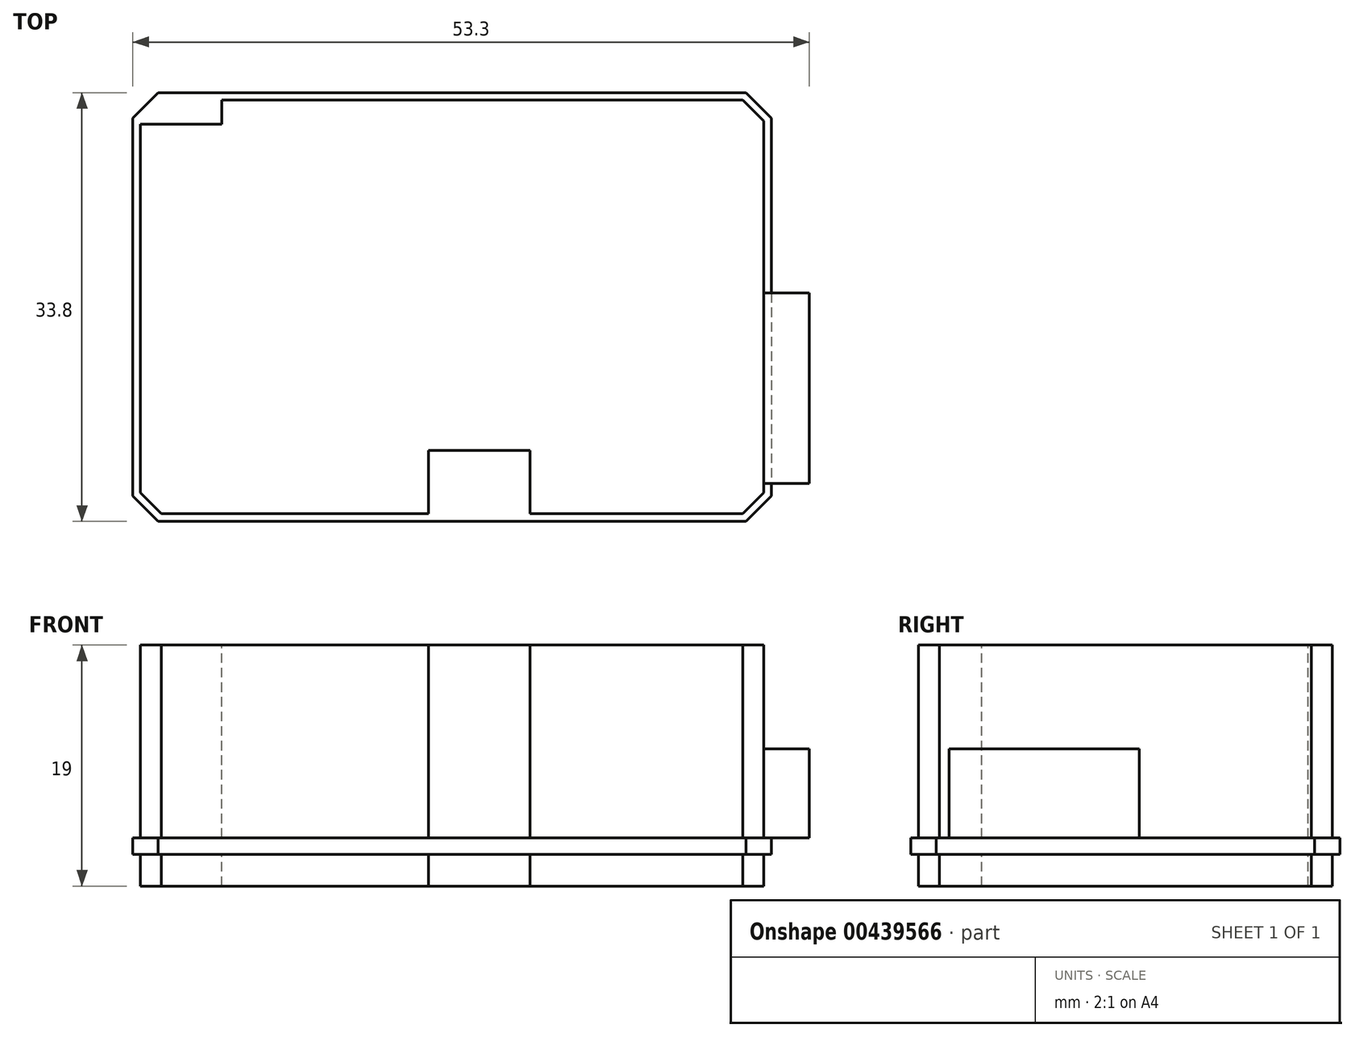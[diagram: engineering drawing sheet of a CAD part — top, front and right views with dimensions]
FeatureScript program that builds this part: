
annotation { "Feature Type Name" : "Feature", "Feature Type Description" : "" }
export const myFeature = defineFeature(function(context is Context, id is Id, definition is map)
    precondition{}
    {
        {
            var Q0;
            Q0=qCreatedBy(makeId("Top.planeOp"),FACE);
            var sketch = newSketch(context, id + "F0", { "sketchPlane" : qUnion([Q0])});
            skLineSegment(sketch, "E0.bottom", {"start": v(22.3, -100) * mm, "end": v(22.3, -133.8) * mm});
            skLineSegment(sketch, "E0.top", {"start": v(-28, -100) * mm, "end": v(-28, -133.8) * mm});
            skLineSegment(sketch, "E0.left", {"start": v(22.3, -100) * mm, "end": v(-28, -100) * mm});
            skLineSegment(sketch, "E0.right", {"start": v(22.3, -133.8) * mm, "end": v(-28, -133.8) * mm});
            skLineSegment(sketch, "E1.bottom", {"start": v(25.3, -115.8) * mm, "end": v(25.3, -130.8) * mm});
            skLineSegment(sketch, "E1.top", {"start": v(11.3, -115.8) * mm, "end": v(11.3, -130.8) * mm});
            skLineSegment(sketch, "E1.left", {"start": v(25.3, -115.8) * mm, "end": v(11.3, -115.8) * mm});
            skLineSegment(sketch, "E1.right", {"start": v(25.3, -130.8) * mm, "end": v(11.3, -130.8) * mm});
            skLineSegment(sketch, "E2", {"start": v(0, 0) * mm, "end": v(0, -100) * mm, "construction": true});
            skSolve(sketch);
        }
        {
            var Q0;
            Q0=makeQuery(id+"F0.imprint","IMPRINT",FACE,{"disambiguationData":[TD([[makeQuery(id+"F0.imprint","IMPRINT",EDGE,{"derivedFrom":sQuery(id+"F0.wireOp",EDGE,"E0.top")}),1.0]])]});
            var Q1;
            {var subQ5=sQuery(id+"F0.wireOp",EDGE,"E1.top");Q1=makeQuery(id+"F0.imprint","IMPRINT",FACE,{"disambiguationData":[TD([[makeQuery(id+"F0.imprint","IMPRINT",EDGE,{"derivedFrom":subQ5}),1.0]])]});}
            extrude(context, id + "F1", {"entities" : qUnion([Q0, Q1]), "oppositeDirection" : true, "depth" : 1.3 * mm});
        }
        {
            var Q0;
            {var subQ5=sQuery(id+"F0.wireOp",EDGE,"E1.bottom");Q0=makeQuery(id+"F0.imprint","IMPRINT",FACE,{"disambiguationData":[TD([[makeQuery(id+"F0.imprint","IMPRINT",EDGE,{"derivedFrom":subQ5}),-1.0]])]});}
            var Q1;
            {var subQ5=sQuery(id+"F0.wireOp",EDGE,"E1.top");Q1=makeQuery(id+"F0.imprint","IMPRINT",FACE,{"disambiguationData":[TD([[makeQuery(id+"F0.imprint","IMPRINT",EDGE,{"derivedFrom":subQ5}),1.0]])]});}
            extrude(context, id + "F2", {"entities" : qUnion([Q0, Q1]), "operationType" : NewBodyOperationType.ADD, "depth" : 7 * mm});
        }
        {
            var Q0;
            Q0=makeQuery(id+"F1.opExtrude","SWEPT_EDGE",EDGE,{"disambiguationData":[OSD([sQuery(id+"F0.wireOp",EDGE,"E0.bottom"),sQuery(id+"F0.wireOp",EDGE,"E0.right")])]});
            var Q1;
            Q1=makeQuery(id+"F1.opExtrude","SWEPT_EDGE",EDGE,{"disambiguationData":[OSD([sQuery(id+"F0.wireOp",EDGE,"E0.top"),sQuery(id+"F0.wireOp",EDGE,"E0.right")])]});
            var Q2;
            Q2=makeQuery(id+"F1.opExtrude","SWEPT_EDGE",EDGE,{"disambiguationData":[OSD([sQuery(id+"F0.wireOp",EDGE,"E0.bottom"),sQuery(id+"F0.wireOp",EDGE,"E0.left")])]});
            var Q3;
            Q3=makeQuery(id+"F1.opExtrude","SWEPT_EDGE",EDGE,{"disambiguationData":[OSD([sQuery(id+"F0.wireOp",EDGE,"E0.top"),sQuery(id+"F0.wireOp",EDGE,"E0.left")])]});
            chamfer(context, id + "F3", {"entities" : qUnion([Q0, Q1, Q2, Q3]), "width" : 2 * mm, "tangentPropagation" : true});
        }
        {
            var Q0;
            Q0=makeQuery(id+"F1.opExtrude","CAP_FACE",FACE,{"disambiguationData":[OSD([sQuery(id+"F0.wireOp",EDGE,"E0.bottom"),sQuery(id+"F0.wireOp",EDGE,"E0.top"),sQuery(id+"F0.wireOp",EDGE,"E0.left"),sQuery(id+"F0.wireOp",EDGE,"E0.right")])],"isStart":false});
            var sketch = newSketch(context, id + "F4", { "sketchPlane" : qUnion([Q0])});
            skLineSegment(sketch, "E3.0.0", {"start": v(-28, 131.8) * mm, "end": v(-28, 102) * mm});
            skLineSegment(sketch, "E3.0.1", {"start": v(-28, 102) * mm, "end": v(-26, 100) * mm});
            skLineSegment(sketch, "E3.0.2", {"start": v(-26, 100) * mm, "end": v(20.3, 100) * mm});
            skLineSegment(sketch, "E3.0.3", {"start": v(20.3, 100) * mm, "end": v(22.3, 102) * mm});
            skLineSegment(sketch, "E3.0.4", {"start": v(22.3, 102) * mm, "end": v(22.3, 131.8) * mm});
            skLineSegment(sketch, "E3.0.5", {"start": v(22.3, 131.8) * mm, "end": v(20.3, 133.8) * mm});
            skLineSegment(sketch, "E3.0.6", {"start": v(20.3, 133.8) * mm, "end": v(-26, 133.8) * mm});
            skLineSegment(sketch, "E3.0.7", {"start": v(-26, 133.8) * mm, "end": v(-28, 131.8) * mm});
            skLineSegment(sketch, "E4.0", {"start": v(-27.4, 131.55) * mm, "end": v(-27.4, 102.5) * mm});
            skLineSegment(sketch, "E4.1", {"start": v(-25.75, 133.2) * mm, "end": v(-27.4, 131.55) * mm});
            skLineSegment(sketch, "E4.3", {"start": v(20.05, 133.2) * mm, "end": v(3.3, 133.2) * mm});
            skLineSegment(sketch, "E4.4", {"start": v(-21, 100.6) * mm, "end": v(20.05, 100.6) * mm});
            skLineSegment(sketch, "E4.5", {"start": v(20.05, 100.6) * mm, "end": v(21.7, 102.25) * mm});
            skLineSegment(sketch, "E4.6", {"start": v(21.7, 102.25) * mm, "end": v(21.7, 131.55) * mm});
            skLineSegment(sketch, "E4.7", {"start": v(21.7, 131.55) * mm, "end": v(20.05, 133.2) * mm});
            skLineSegment(sketch, "E5", {"start": v(-21, 100.6) * mm, "end": v(-21, 102.5) * mm});
            skLineSegment(sketch, "E6", {"start": v(-21, 102.5) * mm, "end": v(-27.4, 102.5) * mm});
            skLineSegment(sketch, "E7", {"start": v(3.3, 133.2) * mm, "end": v(3.3, 128.2) * mm});
            skLineSegment(sketch, "E8", {"start": v(3.3, 128.2) * mm, "end": v(-4.7, 128.2) * mm});
            skLineSegment(sketch, "E9", {"start": v(-4.7, 128.2) * mm, "end": v(-4.7, 133.2) * mm});
            skLineSegment(sketch, "E10.trimOffspring", {"start": v(-4.7, 133.2) * mm, "end": v(-25.75, 133.2) * mm});
            skSolve(sketch);
        }
        {
            var Q0;
            Q0=makeQuery(id+"F4.imprint","IMPRINT",FACE,{"disambiguationData":[TD([[makeQuery(id+"F4.imprint","IMPRINT",EDGE,{"derivedFrom":sQuery(id+"F4.wireOp",EDGE,"E4.0")}),1.0]])]});
            extrude(context, id + "F5", {"entities" : qUnion([Q0]), "operationType" : NewBodyOperationType.ADD, "depth" : 2.5 * mm, "hasSecondDirection" : true, "secondDirectionOppositeDirection" : true, "secondDirectionDepth" : 16.5 * mm});
        }
        {
            var Q0;
            Q0=makeQuery(id+"F1.opExtrude","SWEPT_BODY",BODY,{"disambiguationData":[OSD([sQuery(id+"F0.wireOp",EDGE,"E0.bottom"),sQuery(id+"F0.wireOp",EDGE,"E0.top"),sQuery(id+"F0.wireOp",EDGE,"E0.left"),sQuery(id+"F0.wireOp",EDGE,"E0.right")])]});
            transform(context, id + "F6", {"entities" : qUnion([Q0]), "transformType" : TransformType.TRANSLATION_3D, "dx" : 0 * mm, "dy" : 0 * mm, "dz" : 4 * mm, "makeCopy" : false});
        }
    });
